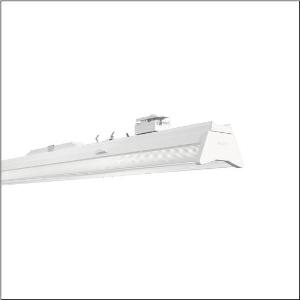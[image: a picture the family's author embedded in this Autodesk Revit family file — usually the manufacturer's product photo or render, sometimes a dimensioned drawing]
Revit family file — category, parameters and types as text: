
# Revit family: licross_11_performance_mo_51td16dn4axg
name_source: partatom
category: Lighting Fixtures
units: mm (PartAtom-declared; Revit-internal decimal feet)

## family parameters
Cut with Voids When Loaded = No
Host = Face
Light Source = No
Part Type = Normal
Room Calculation Point = No
Round Connector Dimension = Use Diameter
Shared = No

## types (1)
- --- (1 x LED, 10110 lm, 57.1 W, 4000K)
    Apparent Load = 57 VA
    CIE Flux Codes = 66 88 96 79 100
    Color Rendering = 80
    Color Temperature = 4000K
    Default Elevation = 1800 mm
    Description = Licross 11 Performance MO, luminaire insert, of sheet steel, galvanised, coil coated, white, length: 1.500mm, width: 120mm, height: 123mm, LED rated luminous flux: 10.110lm, light colour: 840, SDCM (Standard Deviation of Colour Matching)MacAdam ≤ 2 SDCM (initial), control gear: DALI 2, with plug, 5-pole, with phase selection, mains connection: 220..240V, AC, 50/60Hz, rated input power: 57W, internal wiring halogen-free, primary light control with lens, of plastic, primary optical cover: cover, of PMMA, light emission: direct/indirect distribution, primary light characteristic: symmetric, protection rating (complete): IP54, insulation class (complete): insulation class I (protective earthing), certification: CE, ENEC, VDE, UKCA, protection symbol: D if used in an environment with non-conductive dust loads with corresponding accessories, impact resistance: IK06, permissible ambient temperature for indoor applications: -25..+35°C, corresponds to IFS (International Featured Standards) requirements for safety and quality in the food industry, reducing of maximum allowable ambient temperature of 5°C with ceiling mounting, LABS conformity tested according to VDMA 24364:2018-05, The light source and the operating device comply with the requirements of the Ecodesign Regulation (EU) 2019/2020 and are replaceable in accordance with this regulation, packaging unit: 1 piece
    Height = 114 mm
    Lamp = 1 x LED
    Lamp Light Flux = 10110 lm
    Lamp Power = 57.1 W
    Lamp count = 1
    Length = 1500 mm
    Luminous efficacy = 177 lm/W
    Manufacturer = Siteco
    ModVariant = No
    Model = 51TD16DN4AXG
    Mounting Place = Ceiling
    Mounting Type = Pendant
    Number of Poles = 1
    OnlyDefault = Yes
    Power Factor = 1
    Product Name = Licross 11 Performance MO
    Product group = luminaire insert | ceiling pendant
    ProductGroupID = 901
    Protection Class = Protection class I
    Protection Degree = IP 54
    RLX_Detail_Level = 1
    RLX_Emergency_Light_Flux = 0 lm
    RLX_Emergency_Type = 0
    RLX_Emergency_Type_DB = No
    RlxData = <blob elided: 34305 chars, md5=4f99f382>
    Socket = socket
    Standby Power = 0 W
    System Light Flux = 10110 lm
    System Power = 57 W
    Type Comments = factory setting: luminous flux: 100 % | dim-lin: 254 | 378 mA
    Type Image = l_1256138.jpg
    URL = http://relux.com
    VarID = @adj_104407
    Voltage = 0 V
    Weight = 0.00 kg
    Width = 120 mm

## geometry (parser evidence)
native form markers: Blend x4, Sweep x11
no freeform markers — native parametric forms only
